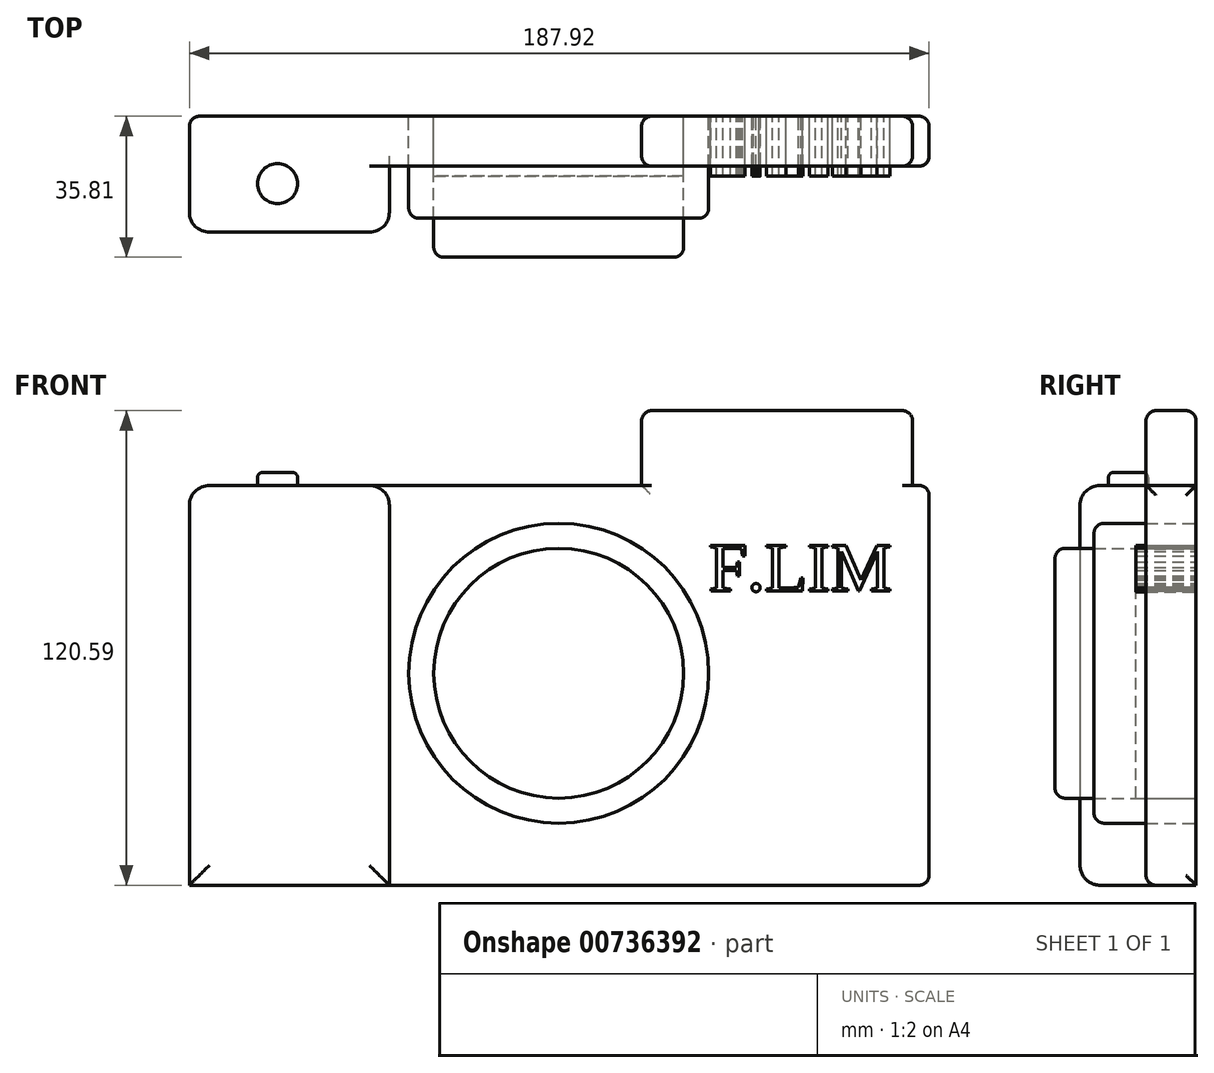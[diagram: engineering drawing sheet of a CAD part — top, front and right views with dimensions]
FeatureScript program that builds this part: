
annotation { "Feature Type Name" : "Feature", "Feature Type Description" : "" }
export const myFeature = defineFeature(function(context is Context, id is Id, definition is map)
    precondition{}
    {
        {
            var Q0;
            Q0=qCreatedBy(makeId("Front.planeOp"),FACE);
            var sketch = newSketch(context, id + "F0", { "sketchPlane" : qUnion([Q0])});
            skLineSegment(sketch, "E0.bottom", {"start": v(-93.83, 47.72) * mm, "end": v(94.09, 47.72) * mm});
            skLineSegment(sketch, "E0.top", {"start": v(-93.83, -53.88) * mm, "end": v(94.09, -53.88) * mm});
            skLineSegment(sketch, "E0.left", {"start": v(-93.83, 47.72) * mm, "end": v(-93.83, -53.88) * mm});
            skLineSegment(sketch, "E0.right", {"start": v(94.09, 47.72) * mm, "end": v(94.09, -53.88) * mm});
            skLineSegment(sketch, "E1.bottom", {"start": v(21.06, 47.72) * mm, "end": v(89.85, 47.72) * mm});
            skLineSegment(sketch, "E1.top", {"start": v(21.06, 66.7) * mm, "end": v(89.85, 66.7) * mm});
            skLineSegment(sketch, "E1.left", {"start": v(21.06, 47.72) * mm, "end": v(21.06, 66.7) * mm});
            skLineSegment(sketch, "E1.right", {"start": v(89.85, 47.72) * mm, "end": v(89.85, 66.7) * mm});
            skSolve(sketch);
        }
        {
            var Q0;
            Q0=qCreatedBy(makeId("Front.planeOp"),FACE);
            var sketch = newSketch(context, id + "F1", { "sketchPlane" : qUnion([Q0])});
            skCircle(sketch, "E2", {"center": v(0, 0) * mm, "radius": 38.1 * mm});
            skSolve(sketch);
        }
        {
            var Q0;
            Q0=qCreatedBy(makeId("Front.planeOp"),FACE);
            var sketch = newSketch(context, id + "F2", { "sketchPlane" : qUnion([Q0])});
            skCircle(sketch, "E3", {"center": v(0, 0) * mm, "radius": 31.75 * mm});
            skText(sketch, "E4", { "text": "F.LIM", "fontName": "Tinos-Regular.ttf"});
            skLineSegment(sketch, "E5", {"start": v(85.24, 37.03) * mm, "end": v(85.24, 6.18) * mm});
            const initialGuessF2  = {"E4": [0.0381, 0.02095, 1, 0, 0.0127]};
            skSetInitialGuess(sketch, initialGuessF2);
            skSolve(sketch);
        }
        {
            var Q0;
            Q0=qCreatedBy(makeId("Front.planeOp"),FACE);
            var sketch = newSketch(context, id + "F3", { "sketchPlane" : qUnion([Q0])});
            skLineSegment(sketch, "E6.bottom", {"start": v(-93.83, 47.72) * mm, "end": v(-43.03, 47.72) * mm});
            skLineSegment(sketch, "E6.top", {"start": v(-93.83, -53.88) * mm, "end": v(-43.03, -53.88) * mm});
            skLineSegment(sketch, "E6.left", {"start": v(-93.83, 47.72) * mm, "end": v(-93.83, -53.88) * mm});
            skLineSegment(sketch, "E6.right", {"start": v(-43.03, 47.72) * mm, "end": v(-43.03, -53.88) * mm});
            skSolve(sketch);
        }
        {
            var Q0;
            Q0=makeQuery(id+"F0.imprint","IMPRINT",FACE,{"disambiguationData":[TD([[makeQuery(id+"F0.imprint","IMPRINT",EDGE,{"derivedFrom":sQuery(id+"F0.wireOp",EDGE,"E1.top")}),-1.0]])]});
            var Q1;
            Q1=makeQuery(id+"F0.imprint","IMPRINT",FACE,{"disambiguationData":[TD([[makeQuery(id+"F0.imprint","IMPRINT",EDGE,{"derivedFrom":sQuery(id+"F0.wireOp",EDGE,"E0.top")}),1.0]])]});
            var Q2;
            Q2 = qSketchRegion(id + "F1", true);
            extrude(context, id + "F4", {"entities" : qUnion([Q0, Q1, Q2]), "depth" : 12.7 * mm, "offsetDistance" : 25.4 * mm});
        }
        {
            var Q0;
            Q0=makeQuery(id+"F1.imprint","IMPRINT",FACE,{"disambiguationData":[TD([[makeQuery(id+"F1.imprint","IMPRINT",EDGE,{"derivedFrom":sQuery(id+"F1.wireOp",EDGE,"E2")}),1.0]])]});
            extrude(context, id + "F5", {"entities" : qUnion([Q0]), "depth" : 25.9 * mm, "offsetDistance" : 25.4 * mm});
        }
        {
            var Q0;
            Q0=makeQuery(id+"F3.imprint","IMPRINT",FACE,{"disambiguationData":[TD([[makeQuery(id+"F3.imprint","IMPRINT",EDGE,{"derivedFrom":sQuery(id+"F3.wireOp",EDGE,"E6.bottom")}),-1.0]])]});
            extrude(context, id + "F6", {"entities" : qUnion([Q0]), "operationType" : NewBodyOperationType.ADD, "depth" : 29.46 * mm, "offsetDistance" : 25.4 * mm});
        }
        {
            var Q0;
            Q0=makeQuery(id+"F2.imprint","IMPRINT",FACE,{"disambiguationData":[TD([[makeQuery(id+"F2.imprint","IMPRINT",EDGE,{"derivedFrom":sQuery(id+"F2.wireOp",EDGE,"E3")}),1.0]])]});
            extrude(context, id + "F7", {"entities" : qUnion([Q0]), "depth" : 35.81 * mm, "offsetDistance" : 25.4 * mm});
        }
        {
            var Q0;
            Q0 = qSketchRegion(id + "F2", true);
            extrude(context, id + "F8", {"entities" : qUnion([Q0]), "depth" : 15.24 * mm, "offsetDistance" : 25.4 * mm});
        }
        {
            var Q0;
            Q0=makeQuery(id+"F0.imprint","IMPRINT",FACE,{"disambiguationData":[TD([[makeQuery(id+"F0.imprint","IMPRINT",EDGE,{"derivedFrom":sQuery(id+"F0.wireOp",EDGE,"E1.top")}),-1.0]])]});
            extrude(context, id + "F9", {"entities" : qUnion([Q0]), "operationType" : NewBodyOperationType.ADD, "depth" : 12.7 * mm, "offsetDistance" : 25.4 * mm});
        }
        {
            var Q0;
            Q0=makeQuery(id+"F6.opExtrude","CAP_EDGE",EDGE,{"disambiguationData":[OSD([sQuery(id+"F3.wireOp",EDGE,"E6.bottom")])],"isStart":false});
            var Q1;
            Q1=makeQuery(id+"F6.opExtrude","SWEPT_EDGE",EDGE,{"disambiguationData":[OSD([sQuery(id+"F3.wireOp",EDGE,"E6.bottom"),sQuery(id+"F3.wireOp",EDGE,"E6.left")])]});
            var Q2;
            Q2=makeQuery(id+"F6.opExtrude","CAP_EDGE",EDGE,{"disambiguationData":[OSD([sQuery(id+"F3.wireOp",EDGE,"E6.left")])],"isStart":false});
            var Q3;
            Q3=makeQuery(id+"F6.opExtrude","CAP_EDGE",EDGE,{"disambiguationData":[OSD([sQuery(id+"F3.wireOp",EDGE,"E6.right")])],"isStart":false});
            var Q4;
            Q4=makeQuery(id+"F6.opExtrude","CAP_EDGE",EDGE,{"disambiguationData":[OSD([sQuery(id+"F3.wireOp",EDGE,"E6.top")])],"isStart":false});
            var Q5;
            Q5=makeQuery(id+"F6.opExtrude","CAP_EDGE",EDGE,{"disambiguationData":[OSD([sQuery(id+"F3.wireOp",EDGE,"E6.top")])],"isStart":true});
            var Q6;
            Q6=makeQuery(id+"F6.opExtrude","SWEPT_EDGE",EDGE,{"disambiguationData":[OSD([sQuery(id+"F3.wireOp",EDGE,"E6.bottom"),sQuery(id+"F3.wireOp",EDGE,"E6.right")])]});
            fillet(context, id + "F10", {"entities" : qUnion([Q0, Q1, Q2, Q3, Q4, Q5, Q6]), "radius" : 5.08 * mm, "tangentPropagation" : true, "allowEdgeOverflow" : false});
        }
        {
            var Q0;
            {var subQ0=sQuery(id+"F0.wireOp",EDGE,"E0.bottom");Q0=makeQuery(id+"F4.opExtrude","CAP_EDGE",EDGE,{"disambiguationData":[OSD([subQ0]),TDD([makeQuery(id+"F0.imprint","IMPRINT",EDGE,{"disambiguationData":[TD([[makeQuery(id+"F0.imprint","INTERSECT",VERTEX,{"derivedFrom":[subQ0,sQuery(id+"F0.wireOp",EDGE,"E0.left")]}),-1.0]])],"derivedFrom":subQ0})])],"isStart":true});}
            var Q1;
            Q1=makeQuery(id+"F4.opExtrude","CAP_EDGE",EDGE,{"disambiguationData":[OSD([sQuery(id+"F0.wireOp",EDGE,"E1.left")])],"isStart":true});
            var Q2;
            Q2=makeQuery(id+"F4.opExtrude","CAP_EDGE",EDGE,{"disambiguationData":[OSD([sQuery(id+"F0.wireOp",EDGE,"E1.top")])],"isStart":true});
            var Q3;
            Q3=makeQuery(id+"F4.opExtrude","CAP_EDGE",EDGE,{"disambiguationData":[OSD([sQuery(id+"F0.wireOp",EDGE,"E1.top")])],"isStart":false});
            var Q4;
            Q4=makeQuery(id+"F4.opExtrude","SWEPT_EDGE",EDGE,{"disambiguationData":[OSD([sQuery(id+"F0.wireOp",EDGE,"E1.top"),sQuery(id+"F0.wireOp",EDGE,"E1.left")])]});
            var Q5;
            Q5=makeQuery(id+"F4.opExtrude","SWEPT_EDGE",EDGE,{"disambiguationData":[OSD([sQuery(id+"F0.wireOp",EDGE,"E1.top"),sQuery(id+"F0.wireOp",EDGE,"E1.right")])]});
            var Q6;
            Q6=makeQuery(id+"F4.opExtrude","CAP_EDGE",EDGE,{"disambiguationData":[OSD([sQuery(id+"F0.wireOp",EDGE,"E1.right")])],"isStart":true});
            var Q7;
            Q7=makeQuery(id+"F4.opExtrude","CAP_EDGE",EDGE,{"disambiguationData":[OSD([sQuery(id+"F0.wireOp",EDGE,"E1.right")])],"isStart":false});
            var Q8;
            Q8=makeQuery(id+"F4.opExtrude","SWEPT_EDGE",EDGE,{"disambiguationData":[OSD([sQuery(id+"F0.wireOp",EDGE,"E0.bottom"),sQuery(id+"F0.wireOp",EDGE,"E0.right")])]});
            var Q9;
            Q9=makeQuery(id+"F4.opExtrude","CAP_EDGE",EDGE,{"disambiguationData":[OSD([sQuery(id+"F0.wireOp",EDGE,"E0.right")])],"isStart":false});
            var Q10;
            Q10=makeQuery(id+"F4.opExtrude","CAP_EDGE",EDGE,{"disambiguationData":[OSD([sQuery(id+"F0.wireOp",EDGE,"E0.right")])],"isStart":true});
            var Q11;
            Q11=makeQuery(id+"F4.opExtrude","SWEPT_EDGE",EDGE,{"disambiguationData":[OSD([sQuery(id+"F0.wireOp",EDGE,"E0.top"),sQuery(id+"F0.wireOp",EDGE,"E0.right")])]});
            var Q12;
            Q12=makeQuery(id+"F4.opExtrude","CAP_EDGE",EDGE,{"disambiguationData":[OSD([sQuery(id+"F0.wireOp",EDGE,"E0.top")])],"isStart":false});
            var Q13;
            Q13=makeQuery(id+"F6.opExtrude","CAP_EDGE",EDGE,{"disambiguationData":[OSD([sQuery(id+"F3.wireOp",EDGE,"E6.top")])],"isStart":true});
            var Q14;
            Q14=makeQuery(id+"F7.opExtrude","CAP_EDGE",EDGE,{"disambiguationData":[OSD([sQuery(id+"F2.wireOp",EDGE,"E3")])],"isStart":false});
            var Q15;
            Q15=makeQuery(id+"F5.opExtrude","CAP_EDGE",EDGE,{"disambiguationData":[OSD([sQuery(id+"F1.wireOp",EDGE,"E2")])],"isStart":false});
            var Q16;
            Q16=makeQuery(id+"F4.opExtrude","SWEPT_EDGE",EDGE,{"disambiguationData":[OSD([sQuery(id+"F0.wireOp",EDGE,"E0.bottom"),sQuery(id+"F0.wireOp",EDGE,"E0.left")])]});
            var Q17;
            Q17=makeQuery(id+"F4.opExtrude","CAP_EDGE",EDGE,{"disambiguationData":[OSD([sQuery(id+"F0.wireOp",EDGE,"E1.left")])],"isStart":false});
            fillet(context, id + "F11", {"entities" : qUnion([Q0, Q1, Q2, Q3, Q4, Q5, Q6, Q7, Q8, Q9, Q10, Q11, Q12, Q13, Q14, Q15, Q16, Q17]), "radius" : 2.54 * mm, "tangentPropagation" : true, "allowEdgeOverflow" : false});
        }
        {
            var Q0;
            Q0=makeQuery(id+"F6.opExtrude","SWEPT_FACE",FACE,{"disambiguationData":[OSD([sQuery(id+"F3.wireOp",EDGE,"E6.bottom")])]});
            var sketch = newSketch(context, id + "F12", { "sketchPlane" : qUnion([Q0])});
            skCircle(sketch, "E7", {"center": v(-71.44, -17.15) * mm, "radius": 5.08 * mm});
            skLineSegment(sketch, "E8", {"start": v(-76.52, -3.2) * mm, "end": v(-76.52, -17.25) * mm});
            skSolve(sketch);
        }
        {
            var Q0;
            Q0=makeQuery(id+"F12.imprint","IMPRINT",FACE,{"disambiguationData":[TD([[makeQuery(id+"F12.imprint","IMPRINT",EDGE,{"derivedFrom":sQuery(id+"F12.wireOp",EDGE,"E7")}),1.0]])]});
            extrude(context, id + "F13", {"entities" : qUnion([Q0]), "depth" : 3.3 * mm, "offsetDistance" : 25.4 * mm});
        }
        {
            var Q0;
            Q0=makeQuery(id+"F13.opExtrude","CAP_FACE",FACE,{"disambiguationData":[OSD([sQuery(id+"F12.wireOp",EDGE,"E7")])],"isStart":false});
            fillet(context, id + "F14", {"entities" : qUnion([Q0]), "radius" : 1.27 * mm, "tangentPropagation" : true, "allowEdgeOverflow" : false});
        }
        {
            var Q0;
            Q0=qCreatedBy(makeId("Top.planeOp"),FACE);
            var sketch = newSketch(context, id + "F15", { "sketchPlane" : qUnion([Q0])});
            skCircle(sketch, "E9", {"center": v(-48.74, -10.15) * mm, "radius": 3.52 * mm});
            skSolve(sketch);
        }
        {
            var Q0;
            {var subQ0=sQuery(id+"F0.wireOp",EDGE,"E0.bottom");Q0=makeQuery(id+"F6.boolean.opBoolean","MERGE",FACE,{"derivedFrom":[makeQuery(id+"F4.opExtrude","SWEPT_FACE",FACE,{"disambiguationData":[OSD([subQ0]),TDD([makeQuery(id+"F0.imprint","IMPRINT",EDGE,{"disambiguationData":[TD([[makeQuery(id+"F0.imprint","INTERSECT",VERTEX,{"derivedFrom":[subQ0,sQuery(id+"F0.wireOp",EDGE,"E0.left")]}),-1.0]])],"derivedFrom":subQ0})])]}),makeQuery(id+"F6.opExtrude","SWEPT_FACE",FACE,{"disambiguationData":[OSD([sQuery(id+"F3.wireOp",EDGE,"E6.bottom")])]})]});}
            extrude(context, id + "F16", {"entities" : qUnion([Q0]), "operationType" : NewBodyOperationType.ADD, "oppositeDirection" : true, "depth" : 0.76 * mm, "offsetDistance" : 25.4 * mm});
        }
        {
            var Q0;
            Q0=sQuery(id+"F15.wireOp",EDGE,"E9");
            extrude(context, id + "F17", {"bodyType" : ToolBodyType.SURFACE, "surfaceEntities" : qUnion([Q0]), "depth" : 38.35 * mm, "offsetDistance" : 25.4 * mm});
        }
    });
